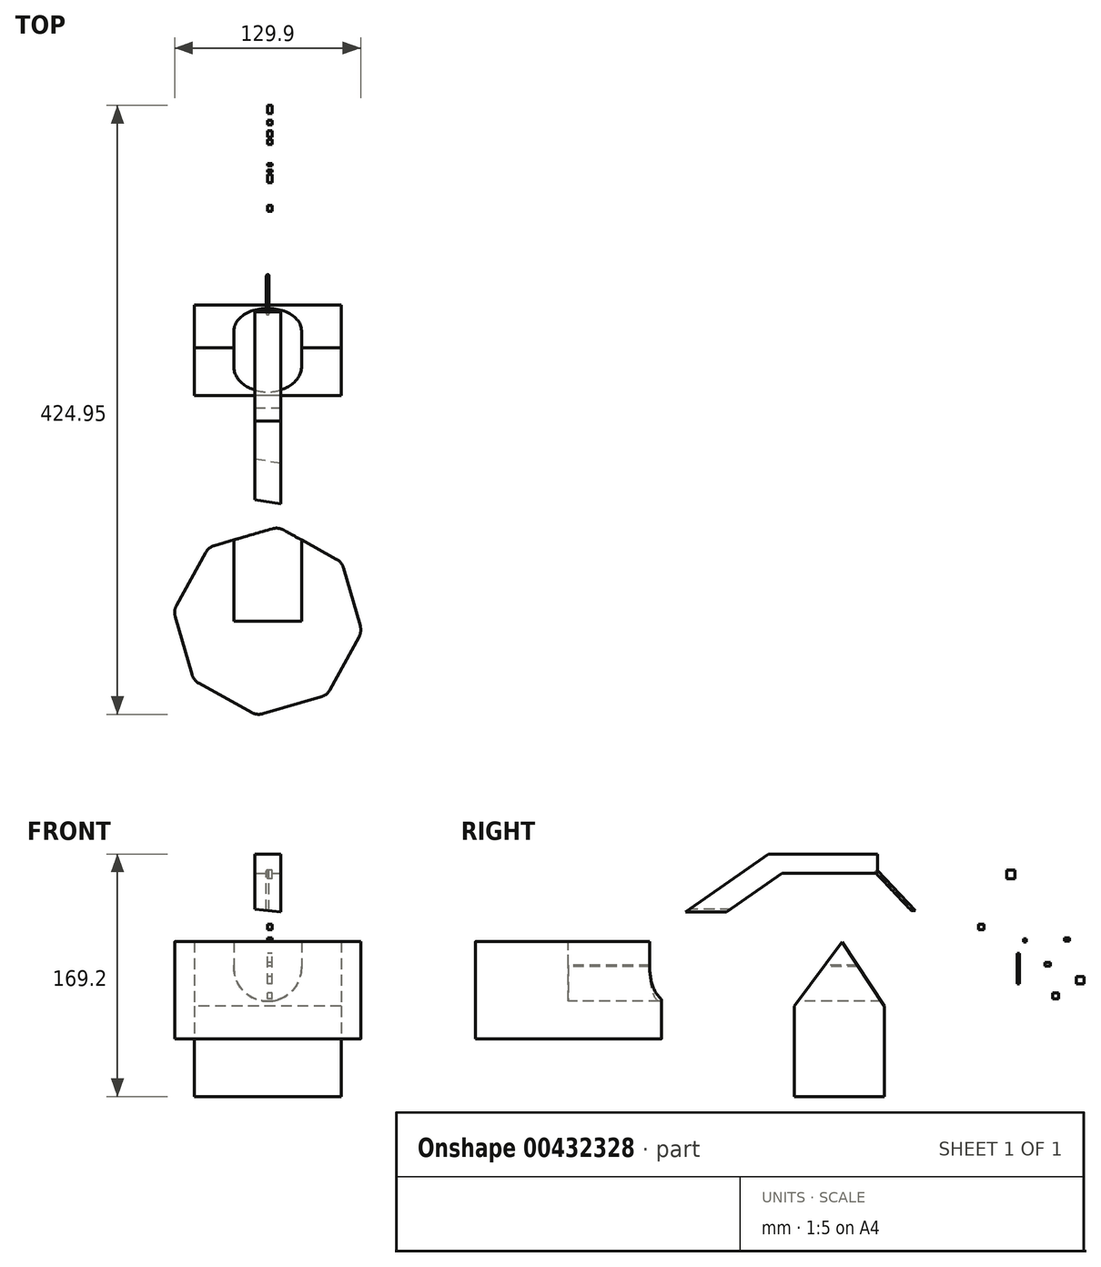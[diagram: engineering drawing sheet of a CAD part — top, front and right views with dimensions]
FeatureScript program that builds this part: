
annotation { "Feature Type Name" : "Feature", "Feature Type Description" : "" }
export const myFeature = defineFeature(function(context is Context, id is Id, definition is map)
    precondition{}
    {
        {
            var Q0;
            Q0=qCreatedBy(makeId("Top.planeOp"),FACE);
            var sketch = newSketch(context, id + "F0", { "sketchPlane" : qUnion([Q0])});
            skCircle(sketch, "E0.cCircle", {"center": v(0, 0) * mm, "radius": 61.1 * mm, "construction": true});
            skLineSegment(sketch, "E0.0", {"start": v(37.23, -52.84) * mm, "end": v(-3.31, -64.55) * mm});
            skLineSegment(sketch, "E0.1", {"start": v(-11.04, -63.69) * mm, "end": v(-47.99, -43.3) * mm});
            skLineSegment(sketch, "E0.2", {"start": v(-52.84, -37.23) * mm, "end": v(-64.55, 3.31) * mm});
            skLineSegment(sketch, "E0.3", {"start": v(-63.69, 11.04) * mm, "end": v(-43.3, 47.99) * mm});
            skLineSegment(sketch, "E0.4", {"start": v(-37.23, 52.84) * mm, "end": v(3.31, 64.55) * mm});
            skLineSegment(sketch, "E0.5", {"start": v(11.04, 63.69) * mm, "end": v(47.99, 43.3) * mm});
            skLineSegment(sketch, "E0.6", {"start": v(52.84, 37.23) * mm, "end": v(64.55, -3.31) * mm});
            skLineSegment(sketch, "E0.7", {"start": v(63.69, -11.04) * mm, "end": v(43.3, -47.99) * mm});
            skPoint(sketch, "E0.0.midPoint", {"position": v(16.96, -58.7) * mm});
            skPoint(sketch, "E1.visualSharp", {"position": v(51.67, 41.27) * mm});
            skArc(sketch, "E1.filletArc", {"start": v(52.84, 37.23) * mm, "mid": v(51.02, 40.75) * mm, "end": v(47.99, 43.3) * mm});
            skPoint(sketch, "E2.visualSharp", {"position": v(65.72, -7.36) * mm});
            skArc(sketch, "E2.filletArc", {"start": v(63.69, -11.04) * mm, "mid": v(64.89, -7.26) * mm, "end": v(64.55, -3.31) * mm});
            skPoint(sketch, "E3.visualSharp", {"position": v(41.27, -51.67) * mm});
            skArc(sketch, "E3.filletArc", {"start": v(37.23, -52.84) * mm, "mid": v(40.75, -51.02) * mm, "end": v(43.3, -47.99) * mm});
            skPoint(sketch, "E4.visualSharp", {"position": v(-7.36, -65.72) * mm});
            skArc(sketch, "E4.filletArc", {"start": v(-11.04, -63.69) * mm, "mid": v(-7.26, -64.89) * mm, "end": v(-3.31, -64.55) * mm});
            skPoint(sketch, "E5.visualSharp", {"position": v(-51.67, -41.27) * mm});
            skArc(sketch, "E5.filletArc", {"start": v(-52.84, -37.23) * mm, "mid": v(-51.02, -40.75) * mm, "end": v(-47.99, -43.3) * mm});
            skPoint(sketch, "E6.visualSharp", {"position": v(-65.72, 7.36) * mm});
            skArc(sketch, "E6.filletArc", {"start": v(-63.69, 11.04) * mm, "mid": v(-64.89, 7.26) * mm, "end": v(-64.55, 3.31) * mm});
            skPoint(sketch, "E7.visualSharp", {"position": v(7.36, 65.72) * mm});
            skArc(sketch, "E7.filletArc", {"start": v(11.04, 63.69) * mm, "mid": v(7.26, 64.89) * mm, "end": v(3.31, 64.55) * mm});
            skPoint(sketch, "E8.visualSharp", {"position": v(-41.27, 51.67) * mm});
            skArc(sketch, "E8.filletArc", {"start": v(-37.23, 52.84) * mm, "mid": v(-40.75, 51.02) * mm, "end": v(-43.3, 47.99) * mm});
            skSolve(sketch);
        }
        {
            var Q0;
            Q0 = qSketchRegion(id + "F0", true);
            extrude(context, id + "F1", {"entities" : qUnion([Q0]), "depth" : 67.82 * mm});
        }
        {
            var Q0;
            Q0=makeQuery(id+"F1.opExtrude","CAP_FACE",FACE,{"disambiguationData":[OSD([sQuery(id+"F0.wireOp",EDGE,"E0.0"),sQuery(id+"F0.wireOp",EDGE,"E0.1"),sQuery(id+"F0.wireOp",EDGE,"E0.2"),sQuery(id+"F0.wireOp",EDGE,"E0.3"),sQuery(id+"F0.wireOp",EDGE,"E0.4"),sQuery(id+"F0.wireOp",EDGE,"E0.5"),sQuery(id+"F0.wireOp",EDGE,"E0.6"),sQuery(id+"F0.wireOp",EDGE,"E0.7"),sQuery(id+"F0.wireOp",EDGE,"E1.filletArc"),sQuery(id+"F0.wireOp",EDGE,"E2.filletArc"),sQuery(id+"F0.wireOp",EDGE,"E3.filletArc"),sQuery(id+"F0.wireOp",EDGE,"E4.filletArc"),sQuery(id+"F0.wireOp",EDGE,"E5.filletArc"),sQuery(id+"F0.wireOp",EDGE,"E6.filletArc"),sQuery(id+"F0.wireOp",EDGE,"E7.filletArc"),sQuery(id+"F0.wireOp",EDGE,"E8.filletArc")])],"isStart":false});
            var sketch = newSketch(context, id + "F2", { "sketchPlane" : qUnion([Q0])});
            skLineSegment(sketch, "E9", {"start": v(29.69, 83.28) * mm, "end": v(-35.27, 83.28) * mm});
            skSolve(sketch);
        }
        {
            var Q0;
            Q0=sQuery(id+"F2.wireOp",EDGE,"E9");
            cPlane(context, id + "F3", {"entities" : qUnion([Q0]), "cplaneType" : CPlaneType.LINE_ANGLE, "offset" : 25.4 * mm, "angle" : 35 * degree, "oppositeDirection" : true, "width" : 152.4 * mm, "height" : 152.4 * mm});
        }
        {
            var Q0;
            Q0=qCreatedBy(id+"F3.planeOp",FACE);
            var sketch = newSketch(context, id + "F4", { "sketchPlane" : qUnion([Q0])});
            skLineSegment(sketch, "E10.bottom", {"start": v(-9.11, 9.15) * mm, "end": v(9.11, 9.15) * mm});
            skLineSegment(sketch, "E10.top", {"start": v(-9.11, 25.57) * mm, "end": v(9.11, 25.57) * mm});
            skLineSegment(sketch, "E10.left", {"start": v(-9.11, 9.15) * mm, "end": v(-9.11, 25.57) * mm});
            skLineSegment(sketch, "E10.right", {"start": v(9.11, 9.15) * mm, "end": v(9.11, 25.57) * mm});
            skPoint(sketch, "E10.middle", {"position": v(0, 17.36) * mm});
            skSolve(sketch);
        }
        {
            var Q0;
            Q0 = qSketchRegion(id + "F4", true);
            extrude(context, id + "F5", {"entities" : qUnion([Q0]), "operationType" : NewBodyOperationType.ADD, "depth" : 35.05 * mm, "hasSecondDirection" : true, "secondDirectionOppositeDirection" : true, "secondDirectionDepth" : 81.28 * mm});
        }
        {
            var Q0;
            Q0=makeQuery(id+"F5.opExtrude","CAP_VERTEX",VERTEX,{"disambiguationData":[OSD([sQuery(id+"F4.wireOp",EDGE,"E10.top"),sQuery(id+"F4.wireOp",EDGE,"E10.right")])],"isStart":true});
            var Q1;
            Q1=qCreatedBy(makeId("Front.planeOp"),FACE);
            cPlane(context, id + "F6", {"entities" : qUnion([Q0, Q1]), "cplaneType" : CPlaneType.PLANE_POINT, "offset" : 25.4 * mm, "width" : 152.4 * mm, "height" : 152.4 * mm});
        }
        {
            var Q0;
            Q0=qCreatedBy(id+"F6.planeOp",FACE);
            var sketch = newSketch(context, id + "F7", { "sketchPlane" : qUnion([Q0])});
            skLineSegment(sketch, "E11.0.0", {"start": v(-9.11, 129) * mm, "end": v(9.11, 129) * mm});
            skLineSegment(sketch, "E11.0.1", {"start": v(9.11, 129) * mm, "end": v(9.11, 115.56) * mm});
            skLineSegment(sketch, "E11.0.2", {"start": v(9.11, 115.56) * mm, "end": v(-9.11, 115.56) * mm});
            skLineSegment(sketch, "E11.0.3", {"start": v(-9.11, 115.56) * mm, "end": v(-9.11, 129) * mm});
            skSolve(sketch);
        }
        {
            var Q0;
            Q0 = qSketchRegion(id + "F7", true);
            extrude(context, id + "F8", {"entities" : qUnion([Q0]), "operationType" : NewBodyOperationType.ADD, "oppositeDirection" : true, "depth" : 76.2 * mm});
        }
        {
            var Q0;
            Q0=qCreatedBy(makeId("Right.planeOp"),FACE);
            var sketch = newSketch(context, id + "F9", { "sketchPlane" : qUnion([Q0])});
            skArc(sketch, "E12", {"start": v(262.87, 64.58) * mm, "mid": v(263.09, 35.04) * mm, "end": v(292.63, 34.55) * mm});
            skLineSegment(sketch, "E13", {"start": v(214.63, 117.14) * mm, "end": v(278.1, 49.92) * mm});
            skLineSegment(sketch, "E14.0", {"start": v(213.9, 116.44) * mm, "end": v(262.87, 64.58) * mm});
            skLineSegment(sketch, "E15", {"start": v(278.1, 49.92) * mm, "end": v(292.63, 34.55) * mm});
            skLineSegment(sketch, "E16", {"start": v(213.9, 116.44) * mm, "end": v(214.63, 117.14) * mm});
            skSolve(sketch);
        }
        {
            var Q0;
            Q0 = qSketchRegion(id + "F9", true);
            var Q1;
            Q1 = qConstructionFilter(qBodyType(qCreatedBy(id + "F9" ,EDGE), BodyType.WIRE), ConstructionObject.NO);
            var Q2;
            Q2=sQuery(id+"F9.wireOp",EDGE,"E13");
            revolve(context, id + "F10", {"entities" : qUnion([Q0]), "surfaceEntities" : qUnion([Q1]), "axis" : qUnion([Q2]), "revolveType" : RevolveType.FULL});
        }
        {
            var Q0;
            Q0=qCreatedBy(makeId("Right.planeOp"),FACE);
            var sketch = newSketch(context, id + "F11", { "sketchPlane" : qUnion([Q0])});
            skLineSegment(sketch, "E17.top", {"start": v(220.61, -40.2) * mm, "end": v(157.57, -40.2) * mm});
            skLineSegment(sketch, "E17.left", {"start": v(220.61, 22.84) * mm, "end": v(220.61, -40.2) * mm});
            skLineSegment(sketch, "E17.right", {"start": v(157.57, 22.84) * mm, "end": v(157.57, -40.2) * mm});
            skPoint(sketch, "E17.middle", {"position": v(189.1, -8.68) * mm});
            skLineSegment(sketch, "E18", {"start": v(157.57, 22.84) * mm, "end": v(190.9, 67.7) * mm});
            skLineSegment(sketch, "E19", {"start": v(190.9, 67.7) * mm, "end": v(220.61, 22.84) * mm});
            skSolve(sketch);
        }
        {
            var Q0;
            Q0 = qSketchRegion(id + "F11", true);
            extrude(context, id + "F12", {"entities" : qUnion([Q0]), "endBound" : BoundingType.SYMMETRIC, "depth" : 102.62 * mm});
        }
        {
            var Q0;
            Q0=qCreatedBy(makeId("Front.planeOp"),FACE);
            var sketch = newSketch(context, id + "F13", { "sketchPlane" : qUnion([Q0])});
            skArc(sketch, "E20", {"start": v(-23.58, 51.34) * mm, "mid": v(-0.44, 26.2) * mm, "end": v(23.62, 50.45) * mm});
            skLineSegment(sketch, "E21", {"start": v(23.62, 50.45) * mm, "end": v(23.62, 86.88) * mm});
            skLineSegment(sketch, "E22", {"start": v(-23.58, 51.34) * mm, "end": v(-23.58, 92.27) * mm});
            skLineSegment(sketch, "E23", {"start": v(-23.58, 92.27) * mm, "end": v(23.62, 86.88) * mm});
            skSolve(sketch);
        }
        {
            var Q0;
            Q0 = qSketchRegion(id + "F13", true);
            extrude(context, id + "F14", {"entities" : qUnion([Q0]), "operationType" : NewBodyOperationType.REMOVE, "oppositeDirection" : true, "depth" : 307.34 * mm});
        }
        {
            var Q0;
            Q0=qCreatedBy(makeId("Right.planeOp"),FACE);
            var sketch = newSketch(context, id + "F15", { "sketchPlane" : qUnion([Q0])});
            skLineSegment(sketch, "E24.bottom", {"start": v(311.7, 111.75) * mm, "end": v(305.97, 111.75) * mm});
            skLineSegment(sketch, "E24.top", {"start": v(311.7, 117.88) * mm, "end": v(305.97, 117.88) * mm});
            skLineSegment(sketch, "E24.left", {"start": v(311.7, 111.75) * mm, "end": v(311.7, 117.88) * mm});
            skLineSegment(sketch, "E24.right", {"start": v(305.97, 111.75) * mm, "end": v(305.97, 117.88) * mm});
            skPoint(sketch, "E24.middle", {"position": v(308.83, 114.81) * mm});
            skLineSegment(sketch, "E25.bottom", {"start": v(336.3, 50.91) * mm, "end": v(332.75, 50.91) * mm});
            skLineSegment(sketch, "E25.top", {"start": v(336.3, 53.45) * mm, "end": v(332.75, 53.45) * mm});
            skLineSegment(sketch, "E25.left", {"start": v(336.3, 50.91) * mm, "end": v(336.3, 53.45) * mm});
            skLineSegment(sketch, "E25.right", {"start": v(332.75, 50.91) * mm, "end": v(332.75, 53.45) * mm});
            skPoint(sketch, "E25.middle", {"position": v(334.52, 52.18) * mm});
            skLineSegment(sketch, "E26.bottom", {"start": v(354.43, 38.37) * mm, "end": v(360, 38.37) * mm});
            skLineSegment(sketch, "E26.top", {"start": v(354.43, 43.51) * mm, "end": v(360, 43.51) * mm});
            skLineSegment(sketch, "E26.left", {"start": v(354.43, 38.37) * mm, "end": v(354.43, 43.51) * mm});
            skLineSegment(sketch, "E26.right", {"start": v(360, 38.37) * mm, "end": v(360, 43.51) * mm});
            skPoint(sketch, "E26.middle", {"position": v(357.21, 40.94) * mm});
            skLineSegment(sketch, "E27.bottom", {"start": v(337.93, 27.87) * mm, "end": v(342.22, 27.87) * mm});
            skLineSegment(sketch, "E27.top", {"start": v(337.93, 32.16) * mm, "end": v(342.22, 32.16) * mm});
            skLineSegment(sketch, "E27.left", {"start": v(337.93, 27.87) * mm, "end": v(337.93, 32.16) * mm});
            skLineSegment(sketch, "E27.right", {"start": v(342.22, 27.87) * mm, "end": v(342.22, 32.16) * mm});
            skPoint(sketch, "E27.middle", {"position": v(340.07, 30.02) * mm});
            skLineSegment(sketch, "E28.bottom", {"start": v(317.8, 67.72) * mm, "end": v(319.51, 67.72) * mm});
            skLineSegment(sketch, "E28.top", {"start": v(317.8, 69.86) * mm, "end": v(319.51, 69.86) * mm});
            skLineSegment(sketch, "E28.left", {"start": v(317.8, 67.72) * mm, "end": v(317.8, 69.86) * mm});
            skLineSegment(sketch, "E28.right", {"start": v(319.51, 67.72) * mm, "end": v(319.51, 69.86) * mm});
            skPoint(sketch, "E28.middle", {"position": v(318.65, 68.79) * mm});
            skLineSegment(sketch, "E29.bottom", {"start": v(314.98, 38.37) * mm, "end": v(313.3, 38.37) * mm});
            skLineSegment(sketch, "E29.top", {"start": v(314.98, 59.58) * mm, "end": v(313.3, 59.58) * mm});
            skLineSegment(sketch, "E29.left", {"start": v(314.98, 38.37) * mm, "end": v(314.98, 59.58) * mm});
            skLineSegment(sketch, "E29.right", {"start": v(313.3, 38.37) * mm, "end": v(313.3, 59.58) * mm});
            skPoint(sketch, "E29.middle", {"position": v(314.14, 48.97) * mm});
            skLineSegment(sketch, "E30.bottom", {"start": v(290.16, 80.14) * mm, "end": v(286.13, 80.14) * mm});
            skLineSegment(sketch, "E30.top", {"start": v(290.16, 76.28) * mm, "end": v(286.13, 76.28) * mm});
            skLineSegment(sketch, "E30.left", {"start": v(290.16, 80.14) * mm, "end": v(290.16, 76.28) * mm});
            skLineSegment(sketch, "E30.right", {"start": v(286.13, 80.14) * mm, "end": v(286.13, 76.28) * mm});
            skPoint(sketch, "E30.middle", {"position": v(288.15, 78.21) * mm});
            skLineSegment(sketch, "E31.bottom", {"start": v(346.29, 68.36) * mm, "end": v(349.71, 68.36) * mm});
            skLineSegment(sketch, "E31.top", {"start": v(346.29, 70.5) * mm, "end": v(349.71, 70.5) * mm});
            skLineSegment(sketch, "E31.left", {"start": v(346.29, 68.36) * mm, "end": v(346.29, 70.5) * mm});
            skLineSegment(sketch, "E31.right", {"start": v(349.71, 68.36) * mm, "end": v(349.71, 70.5) * mm});
            skPoint(sketch, "E31.middle", {"position": v(348, 69.43) * mm});
            skSolve(sketch);
        }
        {
            var Q0;
            Q0=makeQuery(id+"F15.imprint","IMPRINT",FACE,{"disambiguationData":[TD([[makeQuery(id+"F15.imprint","IMPRINT",EDGE,{"derivedFrom":sQuery(id+"F15.wireOp",EDGE,"E25.bottom")}),-1.0]])]});
            var Q1;
            Q1=makeQuery(id+"F15.imprint","IMPRINT",FACE,{"disambiguationData":[TD([[makeQuery(id+"F15.imprint","IMPRINT",EDGE,{"derivedFrom":sQuery(id+"F15.wireOp",EDGE,"E26.bottom")}),1.0]])]});
            var Q2;
            Q2=makeQuery(id+"F15.imprint","IMPRINT",FACE,{"disambiguationData":[TD([[makeQuery(id+"F15.imprint","IMPRINT",EDGE,{"derivedFrom":sQuery(id+"F15.wireOp",EDGE,"E27.bottom")}),1.0]])]});
            var Q3;
            Q3=makeQuery(id+"F15.imprint","IMPRINT",FACE,{"disambiguationData":[TD([[makeQuery(id+"F15.imprint","IMPRINT",EDGE,{"derivedFrom":sQuery(id+"F15.wireOp",EDGE,"E28.bottom")}),1.0]])]});
            var Q4;
            Q4=makeQuery(id+"F15.imprint","IMPRINT",FACE,{"disambiguationData":[TD([[makeQuery(id+"F15.imprint","IMPRINT",EDGE,{"derivedFrom":sQuery(id+"F15.wireOp",EDGE,"E29.bottom")}),-1.0]])]});
            var Q5;
            Q5=makeQuery(id+"F15.imprint","IMPRINT",FACE,{"disambiguationData":[TD([[makeQuery(id+"F15.imprint","IMPRINT",EDGE,{"derivedFrom":sQuery(id+"F15.wireOp",EDGE,"E30.bottom")}),1.0]])]});
            var Q6;
            Q6=makeQuery(id+"F15.imprint","IMPRINT",FACE,{"disambiguationData":[TD([[makeQuery(id+"F15.imprint","IMPRINT",EDGE,{"derivedFrom":sQuery(id+"F15.wireOp",EDGE,"E31.bottom")}),1.0]])]});
            var Q7;
            Q7=makeQuery(id+"F15.imprint","IMPRINT",FACE,{"disambiguationData":[TD([[makeQuery(id+"F15.imprint","IMPRINT",EDGE,{"derivedFrom":sQuery(id+"F15.wireOp",EDGE,"E24.bottom")}),-1.0]])]});
            extrude(context, id + "F16", {"entities" : qUnion([Q0, Q1, Q2, Q3, Q4, Q5, Q6, Q7]), "depth" : 3.05 * mm});
        }
    });
